# Revit family: Hager-VOLTA-Flush_mounted-IP30-With_Cover-Without_DIN-Hosted-PL-pl
name_source: partatom
category: Electrical Equipment
units: mm (PartAtom-declared; Revit-internal decimal feet)

## family parameters
Cut with Voids When Loaded = No
Host = Face
Maintain Annotation Orientation = Yes
Panel Configuration = Two Columns, Circuits Across
Part Type = Panelboard
Room Calculation Point = No
Round Connector Dimension = Use Diameter
Shared = No

## types (3) — shared parameters
BC_MODEL_ID = 1547215
BC_OBJECT_ID = 513497
BC_OBJECT_VERSION = #5
Code hager = ADD-EC000214_EU
EF000003 - Sposób montażu = Montaż podtynkowy
EF000007 - Kolor = Biały
EF000008 - Szerokość = 348 mm  [stored 1.14173 ft]
EF000024 - Odporność na promieniowanie UV = No
EF000049 - Głębokość = 98 mm  [stored 0.321522 ft]
EF000116 - Numer RAL = 9010
EF000118 - Z płytą montażową = Yes
EF000218 - Głębokość wbudowania = 89 mm  [stored 0.291995 ft]
EF000846 - Szerokość wbudowania = 315 mm
EF001062 - Wykonanie zgodne z Dyrektywą Kompatybilności Elektromagnetycznej EMC = No
EF001088 - Możliwość rozbudowy = Yes
EF001134 - Szyna DIN = No
EF002950 - Szerokość wyrażona liczbą modułów = 12
EF004462 - Rodzaj zamknięcia = Inne
EF005474 - Stopień ochrony (IP) = IP30
EF006244 - Transparentna pokrywa/drzwi = No
EF006306 - Z zamkiem = No
EF009212 - Wykonanie/rodzaj pokrywy = Z otworem
EF015776 - Listwa zaciskowa uziemienia = Yes
EF015777 - Listwa zaciskowa przewodu neutralnego = Yes
EF015941 - Drzwi przepuszczające sygnał = No
ETIM class code = EC000214
ETIM class name = Small distribution board
HG000002-with door or cover-pl = Yes
HG000003-Range-pl = VOLTA
HG000005-Thickness-pl = 2 mm  [stored 0.00656168 ft]
HG000006-Flush mounted-pl = Yes
HG000009-Double swing door-pl = No
HG000010-Asymmetric doors-pl = No
HG000011-Empty rows from bottom-pl = No
HG000012-Door swing angle-pl = 90.00°
HG000013-Door on the left-pl = No
HG000014-Door on the right-pl = Yes
HG000015-Clearance visibility-pl = Yes
HG000016-Door 3D visibility-pl = Yes
HG000017-Distance between poles-pl = 18 mm  [stored 0.0590551 ft]
HG000060-RAL-number = 9010
HG000099-Onfly Template ID-pl-PL = 507532
HGEF0002950-Szerokość wyrażona liczbą modułów = 12
Manufacturer = Hager
Name = VOLTA-Flush_mounted-IP30-With_Cover-Without_DIN-PL
Name BIM&CO = Electricity
Name hager = ADD_Enclosures_EC000214
Uniformat = Low Tension Service & Dist.
Uniformat code = D501001
zero-valued in all types: Default Elevation, EF000266 - Liczba rzędów, EF001131 - Głębokość wewnętrzna, HG000001-Number of columns-pl, HG000007-Number of empty columns-pl, HG000008-Number of empty rows-pl, HGEF000266-Liczba rzędów

## per-type parameters (varying)
| type | BC_VARIANT_ID | EF000040 - Wysokość | EF000332 - Wysokość wbudowania | HG000004-Manufacturer reference-pl |
| VOLTA-Flush_mounted_W348_H630_D98_12_Modular_Spacing-VU36NWP | 1174403 | 630 mm | 595 mm | VU36NWP |
| VOLTA-Flush_mounted_W348_H755_D98_12_Modular_Spacing-VU48NWP | 1174405 | 755 mm | 720 mm  [stored 2.3622 ft] | VU48NWP |
| VOLTA-Flush_mounted_W348_H880_D98_12_Modular_Spacing-VU60NWP | 1174407 | 880 mm  [stored 2.88714 ft] | 845 mm  [stored 2.77231 ft] | VU60NWP |

note: column(s) folded — value = type name in every type: Reference

note: [stored X ft] marks values corroborated as IEEE doubles in the binary element streams (Revit-internal decimal feet)

## geometry (parser evidence)
native form markers: Sweep x14
no freeform markers — native parametric forms only
